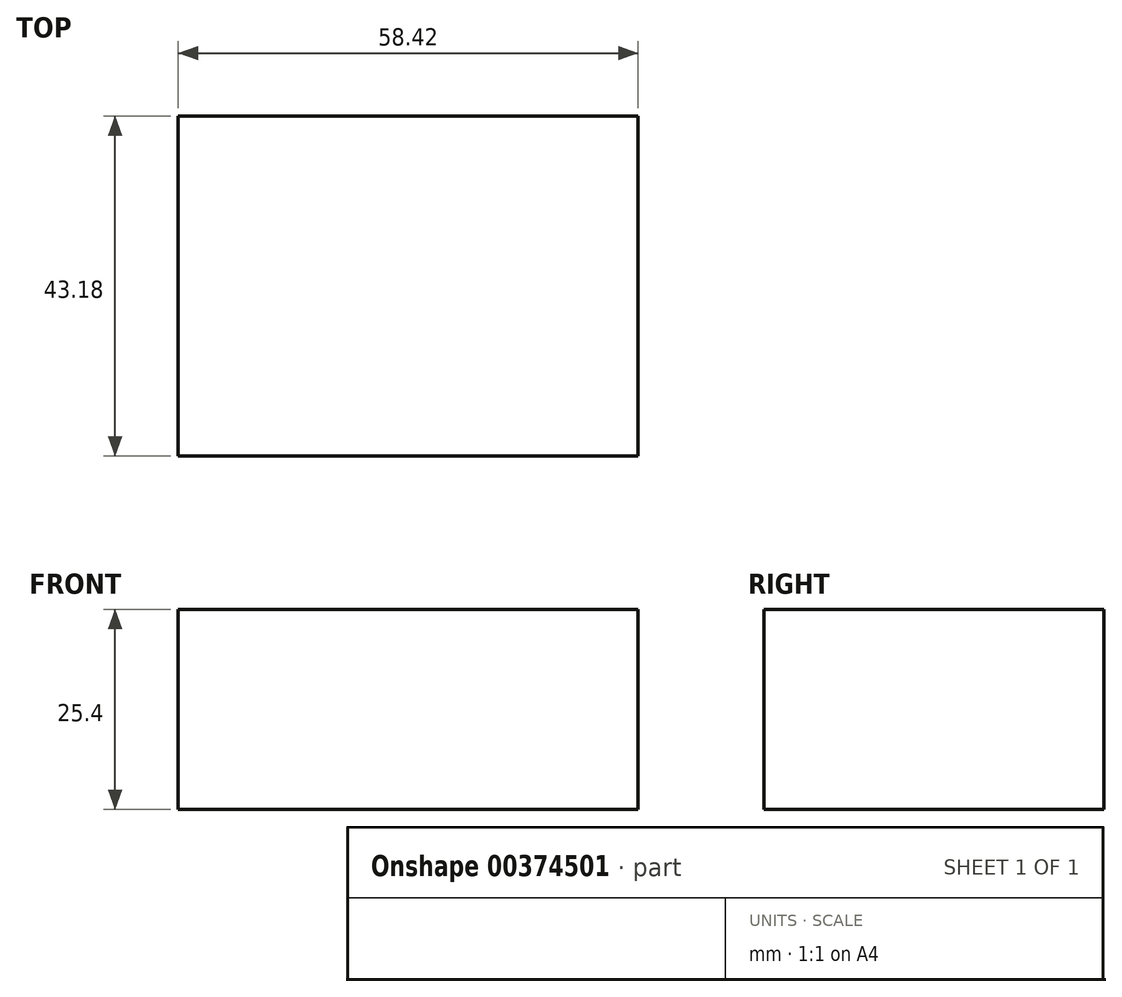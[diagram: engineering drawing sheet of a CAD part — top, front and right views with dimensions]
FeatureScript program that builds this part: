
annotation { "Feature Type Name" : "Feature", "Feature Type Description" : "" }
export const myFeature = defineFeature(function(context is Context, id is Id, definition is map)
    precondition{}
    {
        {
            var Q0;
            Q0=qCreatedBy(makeId("Top.planeOp"),FACE);
            var sketch = newSketch(context, id + "F0", { "sketchPlane" : qUnion([Q0])});
            skLineSegment(sketch, "E0.bottom", {"start": v(-29.2, 21.59) * mm, "end": v(29.21, 21.59) * mm});
            skLineSegment(sketch, "E0.top", {"start": v(-29.21, -21.6) * mm, "end": v(29.2, -21.6) * mm});
            skLineSegment(sketch, "E0.left", {"start": v(-29.2, 21.59) * mm, "end": v(-29.21, -21.6) * mm});
            skLineSegment(sketch, "E0.right", {"start": v(29.21, 21.59) * mm, "end": v(29.2, -21.6) * mm});
            skPoint(sketch, "E0.middle", {"position": v(0, 0) * mm});
            skSolve(sketch);
        }
        {
            var Q0;
            Q0 = qSketchRegion(id + "F0", true);
            extrude(context, id + "F1", {"entities" : qUnion([Q0]), "depth" : 25.4 * mm});
        }
    });
